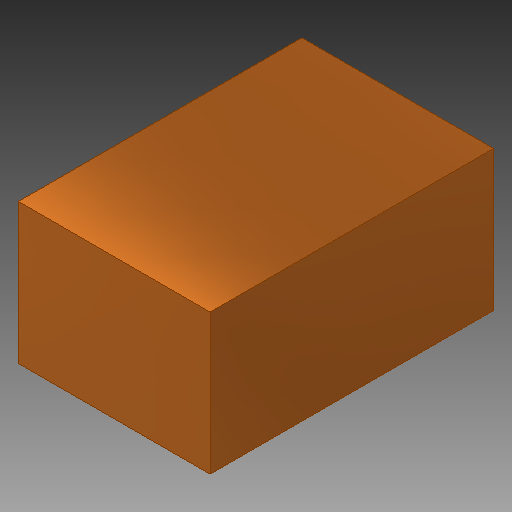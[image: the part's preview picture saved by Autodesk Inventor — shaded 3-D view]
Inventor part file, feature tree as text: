
AUTODESK INVENTOR PART (.ipt)
format: ipt  version: 2017 SP1 (Build 210196100, 196)  size: 91,136 bytes
history: native  units: mm
features: extrude x1, sketch x1
ambient origin geometry x8: Origin, YZ Plane, XZ Plane, XY Plane, X Axis, Y Axis, Z Axis, Center Point
bodies: Solid1 (feature_tree)
feature tree (2):
  extrude  "Extrusion1"  Depth=5.2mm
  sketch  "Sketch1"  dims[d0=7.1mm d1=5.2mm d2=10.5mm d3=0.0mm]
